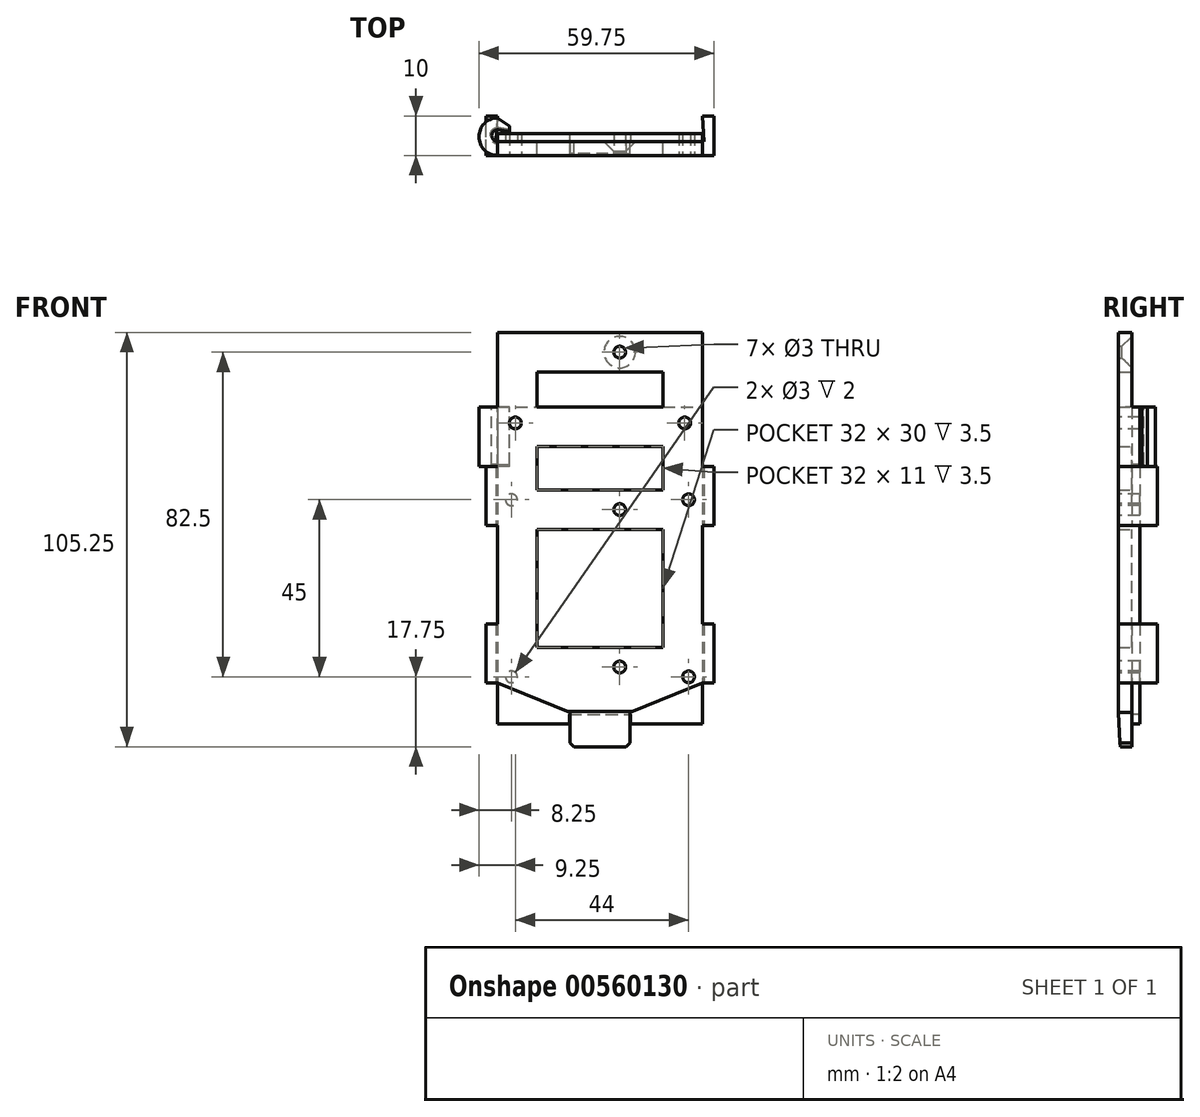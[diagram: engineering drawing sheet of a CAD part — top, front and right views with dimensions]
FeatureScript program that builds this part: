
annotation { "Feature Type Name" : "Feature", "Feature Type Description" : "" }
export const myFeature = defineFeature(function(context is Context, id is Id, definition is map)
    precondition{}
    {
        {
            var Q0;
            Q0=qCreatedBy(makeId("Front.planeOp"),FACE);
            var sketch = newSketch(context, id + "F0", { "sketchPlane" : qUnion([Q0])});
            skLineSegment(sketch, "E0.bottom", {"start": v(26, 40.25) * mm, "end": v(-26, 40.25) * mm});
            skLineSegment(sketch, "E0.top", {"start": v(26, -40.25) * mm, "end": v(-26, -40.25) * mm});
            skLineSegment(sketch, "E0.left", {"start": v(26, 40.25) * mm, "end": v(26, -40.25) * mm});
            skLineSegment(sketch, "E0.right", {"start": v(-26, 40.25) * mm, "end": v(-26, -40.25) * mm});
            skPoint(sketch, "E0.middle", {"position": v(0, 0) * mm});
            skCircle(sketch, "E1", {"center": v(-21.5, 36.25) * mm, "radius": 1.5 * mm});
            skCircle(sketch, "E2", {"center": v(-22.5, 16.75) * mm, "radius": 1.5 * mm});
            skCircle(sketch, "E3", {"center": v(-22.5, -28.25) * mm, "radius": 1.5 * mm});
            skCircle(sketch, "E4.MirrorC", {"center": v(22.5, -28.25) * mm, "radius": 1.5 * mm});
            skCircle(sketch, "E5.MirrorC", {"center": v(22.5, 16.75) * mm, "radius": 1.5 * mm});
            skCircle(sketch, "E6.MirrorC", {"center": v(21.5, 36.25) * mm, "radius": 1.5 * mm});
            skLineSegment(sketch, "E7.bottom", {"start": v(-7.75, -37.75) * mm, "end": v(7.75, -37.75) * mm});
            skLineSegment(sketch, "E7.top", {"start": v(-7.75, -40.25) * mm, "end": v(7.75, -40.25) * mm});
            skLineSegment(sketch, "E7.left", {"start": v(-7.75, -37.75) * mm, "end": v(-7.75, -40.25) * mm});
            skLineSegment(sketch, "E7.right", {"start": v(7.75, -37.75) * mm, "end": v(7.75, -40.25) * mm});
            skCircle(sketch, "E8", {"center": v(5, 14.25) * mm, "radius": 1.5 * mm});
            skCircle(sketch, "E9", {"center": v(5, -25.75) * mm, "radius": 1.5 * mm});
            skSolve(sketch);
        }
        {
            var Q0;
            Q0=makeQuery(id+"F0.imprint","IMPRINT",FACE,{"disambiguationData":[TD([[makeQuery(id+"F0.imprint","IMPRINT",EDGE,{"derivedFrom":sQuery(id+"F0.wireOp",EDGE,"E0.bottom")}),1.0]])]});
            extrude(context, id + "F1", {"entities" : qUnion([Q0]), "oppositeDirection" : true, "depth" : 2 * mm, "offsetDistance" : 25 * mm});
        }
        {
            var Q0;
            Q0=makeQuery(id+"F1.opExtrude","CAP_FACE",FACE,{"disambiguationData":[OSD([sQuery(id+"F0.wireOp",EDGE,"E0.bottom"),sQuery(id+"F0.wireOp",EDGE,"E0.top"),sQuery(id+"F0.wireOp",EDGE,"E0.left"),sQuery(id+"F0.wireOp",EDGE,"E0.right"),sQuery(id+"F0.wireOp",EDGE,"E1"),sQuery(id+"F0.wireOp",EDGE,"E2"),sQuery(id+"F0.wireOp",EDGE,"E3"),sQuery(id+"F0.wireOp",EDGE,"E4.MirrorC"),sQuery(id+"F0.wireOp",EDGE,"E5.MirrorC"),sQuery(id+"F0.wireOp",EDGE,"E6.MirrorC"),sQuery(id+"F0.wireOp",EDGE,"E7.bottom"),sQuery(id+"F0.wireOp",EDGE,"E7.left"),sQuery(id+"F0.wireOp",EDGE,"E7.right")])],"isStart":true});
            var sketch = newSketch(context, id + "F2", { "sketchPlane" : qUnion([Q0])});
            skLineSegment(sketch, "E10.top", {"start": v(-26, 40.25) * mm, "end": v(26, 40.25) * mm});
            skLineSegment(sketch, "E10.left", {"start": v(-26, -29.75) * mm, "end": v(-26, 40.25) * mm});
            skLineSegment(sketch, "E10.right", {"start": v(26, -29.75) * mm, "end": v(26, 40.25) * mm});
            skLineSegment(sketch, "E11", {"start": v(-26, -29.75) * mm, "end": v(-7.65, -37.25) * mm});
            skLineSegment(sketch, "E12", {"start": v(-7.65, -37.25) * mm, "end": v(-7.65, -46) * mm});
            skLineSegment(sketch, "E13", {"start": v(-7.65, -46) * mm, "end": v(0, -46) * mm});
            skLineSegment(sketch, "E14.MirrorCS", {"start": v(26, -29.75) * mm, "end": v(7.65, -37.25) * mm});
            skLineSegment(sketch, "E15.MirrorCS", {"start": v(7.65, -37.25) * mm, "end": v(7.65, -46) * mm});
            skLineSegment(sketch, "E16.MirrorCS", {"start": v(7.65, -46) * mm, "end": v(0, -46) * mm});
            skLineSegment(sketch, "E17.0", {"start": v(-16, -20.75) * mm, "end": v(-16, 30.25) * mm});
            skLineSegment(sketch, "E17.2", {"start": v(-16, 30.25) * mm, "end": v(16, 30.25) * mm});
            skLineSegment(sketch, "E17.5", {"start": v(16, -20.75) * mm, "end": v(16, 9.25) * mm});
            skCircle(sketch, "E18", {"center": v(5, 14.25) * mm, "radius": 1.5 * mm});
            skCircle(sketch, "E19", {"center": v(5, -25.75) * mm, "radius": 1.5 * mm});
            skLineSegment(sketch, "E20.bottom", {"start": v(16, 19.25) * mm, "end": v(-21, 19.25) * mm});
            skLineSegment(sketch, "E20.top", {"start": v(16, 9.25) * mm, "end": v(-16, 9.25) * mm});
            skLineSegment(sketch, "E20.left", {"start": v(16, 19.25) * mm, "end": v(16, 9.25) * mm});
            skLineSegment(sketch, "E21.trimOffspring", {"start": v(16, 19.25) * mm, "end": v(16, 30.25) * mm});
            skLineSegment(sketch, "E22", {"start": v(16, -20.75) * mm, "end": v(-16, -20.75) * mm});
            skSolve(sketch);
        }
        {
            var Q0;
            Q0=qCreatedBy(makeId("Front.planeOp"),FACE);
            var sketch = newSketch(context, id + "F3", { "sketchPlane" : qUnion([Q0])});
            skLineSegment(sketch, "E23.bottom", {"start": v(-26, 40.25) * mm, "end": v(26, 40.25) * mm});
            skLineSegment(sketch, "E23.top", {"start": v(-26, 59.25) * mm, "end": v(26, 59.25) * mm});
            skLineSegment(sketch, "E23.left", {"start": v(-26, 40.25) * mm, "end": v(-26, 59.25) * mm});
            skLineSegment(sketch, "E23.right", {"start": v(26, 40.25) * mm, "end": v(26, 59.25) * mm});
            skCircle(sketch, "E24", {"center": v(5, 54.25) * mm, "radius": 1.5 * mm});
            skLineSegment(sketch, "E25.bottom", {"start": v(-16, 49.25) * mm, "end": v(16, 49.25) * mm});
            skLineSegment(sketch, "E25.top", {"start": v(-16, 40.25) * mm, "end": v(16, 40.25) * mm});
            skLineSegment(sketch, "E25.left", {"start": v(-16, 49.25) * mm, "end": v(-16, 40.25) * mm});
            skLineSegment(sketch, "E25.right", {"start": v(16, 49.25) * mm, "end": v(16, 40.25) * mm});
            skSolve(sketch);
        }
        {
            var Q0;
            {var subQ0=sQuery(id+"F2.wireOp",EDGE,"E13");Q0=makeQuery(id+"F2.imprint","IMPRINT",FACE,{"disambiguationData":[TD([[makeQuery(id+"F2.imprint","IMPRINT",EDGE,{"derivedFrom":subQ0}),1.0]])]});}
            var Q1;
            {var subQ0=sQuery(id+"F2.wireOp",EDGE,"E10.top");Q1=makeQuery(id+"F2.imprint","IMPRINT",FACE,{"disambiguationData":[TD([[makeQuery(id+"F2.imprint","IMPRINT",EDGE,{"derivedFrom":subQ0}),-1.0]])]});}
            var Q2;
            {var subQ6=sQuery(id+"F2.wireOp",EDGE,"E11");Q2=makeQuery(id+"F2.imprint","IMPRINT",FACE,{"disambiguationData":[TD([[makeQuery(id+"F2.imprint","IMPRINT",EDGE,{"derivedFrom":subQ6}),1.0]])]});}
            var Q3;
            {var subQ0=sQuery(id+"F2.wireOp",EDGE,"E12");var subQ1=sQuery(id+"F2.wireOp",EDGE,"E10.bottom");var subQ2=makeQuery(id+"F2.imprint","INTERSECT",VERTEX,{"derivedFrom":[subQ1,subQ0]});Q3=makeQuery(id+"F2.imprint","IMPRINT",FACE,{"disambiguationData":[TD([[makeQuery(id+"F2.imprint","IMPRINT",EDGE,{"disambiguationData":[TD([[subQ2,-1.0]])],"derivedFrom":subQ1}),1.0]])]});}
            var Q4;
            Q4=makeQuery(id+"F2.imprint","IMPRINT",FACE,{"disambiguationData":[TD([[makeQuery(id+"F2.imprint","IMPRINT",EDGE,{"derivedFrom":makeQuery(id+"F1.opExtrude","CAP_EDGE",EDGE,{"disambiguationData":[OSD([sQuery(id+"F0.wireOp",EDGE,"E2")])],"isStart":true})}),1.0]])]});
            var Q5;
            Q5=makeQuery(id+"F2.imprint","IMPRINT",FACE,{"disambiguationData":[TD([[makeQuery(id+"F2.imprint","IMPRINT",EDGE,{"derivedFrom":makeQuery(id+"F1.opExtrude","CAP_EDGE",EDGE,{"disambiguationData":[OSD([sQuery(id+"F0.wireOp",EDGE,"E5.MirrorC")])],"isStart":true})}),-1.0]])]});
            var Q6;
            Q6=makeQuery(id+"F2.imprint","IMPRINT",FACE,{"disambiguationData":[TD([[makeQuery(id+"F2.imprint","IMPRINT",EDGE,{"derivedFrom":sQuery(id+"F2.wireOp",EDGE,"E18")}),-1.0]])]});
            var Q7;
            Q7=makeQuery(id+"F2.imprint","IMPRINT",FACE,{"disambiguationData":[TD([[makeQuery(id+"F2.imprint","IMPRINT",EDGE,{"derivedFrom":makeQuery(id+"F1.opExtrude","CAP_EDGE",EDGE,{"disambiguationData":[OSD([sQuery(id+"F0.wireOp",EDGE,"E4.MirrorC")])],"isStart":true})}),-1.0]])]});
            var Q8;
            Q8=makeQuery(id+"F2.imprint","IMPRINT",FACE,{"disambiguationData":[TD([[makeQuery(id+"F2.imprint","IMPRINT",EDGE,{"derivedFrom":makeQuery(id+"F1.opExtrude","CAP_EDGE",EDGE,{"disambiguationData":[OSD([sQuery(id+"F0.wireOp",EDGE,"E3")])],"isStart":true})}),1.0]])]});
            extrude(context, id + "F4", {"entities" : qUnion([Q0, Q1, Q2, Q3, Q4, Q5, Q6, Q7, Q8]), "depth" : 3.5 * mm, "offsetDistance" : 25 * mm});
        }
        {
            var Q0;
            Q0=makeQuery(id+"F4.opExtrude","CAP_EDGE",EDGE,{"disambiguationData":[OSD([sQuery(id+"F2.wireOp",EDGE,"E13"),sQuery(id+"F2.wireOp",EDGE,"E16.MirrorCS")])],"isStart":false});
            chamfer(context, id + "F5", {"entities" : qUnion([Q0]), "chamferType" : ChamferType.TWO_OFFSETS, "width1" : 9 * mm, "oppositeDirection" : false, "width2" : 0.5 * mm, "tangentPropagation" : true});
        }
        {
            var Q0;
            Q0=makeQuery(id+"F4.opExtrude","SWEPT_EDGE",EDGE,{"disambiguationData":[OSD([sQuery(id+"F2.wireOp",EDGE,"E12"),sQuery(id+"F2.wireOp",EDGE,"E13")])]});
            var Q1;
            Q1=makeQuery(id+"F4.opExtrude","SWEPT_EDGE",EDGE,{"disambiguationData":[OSD([sQuery(id+"F2.wireOp",EDGE,"E15.MirrorCS"),sQuery(id+"F2.wireOp",EDGE,"E16.MirrorCS")])]});
            chamfer(context, id + "F6", {"entities" : qUnion([Q0, Q1]), "width" : 1 * mm, "tangentPropagation" : true});
        }
        {
            var Q0;
            Q0=makeQuery(id+"F4.opExtrude","SWEPT_FACE",FACE,{"disambiguationData":[OSD([sQuery(id+"F2.wireOp",EDGE,"E10.top")])]});
            var sketch = newSketch(context, id + "F7", { "sketchPlane" : qUnion([Q0])});
            skLineSegment(sketch, "E26", {"start": v(-23, 2.5) * mm, "end": v(-25.9, 3) * mm});
            skArc(sketch, "E27", {"start": v(-26, 6) * mm, "mid": v(-30.75, 1.25) * mm, "end": v(-26, -3.5) * mm});
            skLineSegment(sketch, "E28", {"start": v(-23, 2.5) * mm, "end": v(-23, 3.95) * mm});
            skLineSegment(sketch, "E29", {"start": v(-23, 3.95) * mm, "end": v(-26, 6) * mm});
            skPoint(sketch, "E30.center.orphan", {"position": v(-26, 1.5) * mm});
            skArc(sketch, "E31", {"start": v(-25.9, 3) * mm, "mid": v(-27.5, 1.55) * mm, "end": v(-26, 0) * mm});
            skArc(sketch, "E32.MirrorCS", {"start": v(26, 6) * mm, "mid": v(30.75, 1.25) * mm, "end": v(26, -3.5) * mm});
            skArc(sketch, "E33.MirrorCS", {"start": v(25.9, 3) * mm, "mid": v(27.5, 1.55) * mm, "end": v(26, 0) * mm});
            skLineSegment(sketch, "E34.MirrorCS", {"start": v(23, 2.5) * mm, "end": v(25.9, 3) * mm});
            skLineSegment(sketch, "E35.MirrorCS", {"start": v(23, 3.95) * mm, "end": v(26, 6) * mm});
            skLineSegment(sketch, "E36.MirrorCS", {"start": v(23, 2.5) * mm, "end": v(23, 3.95) * mm});
            skSolve(sketch);
        }
        {
            var Q0;
            Q0=qSketchRegion(id+"F7",true);
            var Q1;
            Q1=makeQuery(id+"F7.imprint","IMPRINT",FACE,{"disambiguationData":[TD([[makeQuery(id+"F7.imprint","IMPRINT",EDGE,{"derivedFrom":sQuery(id+"F7.wireOp",EDGE,"E26")}),-1.0]])]});
            var Q2;
            Q2=makeQuery(id+"F7.imprint","IMPRINT",FACE,{"disambiguationData":[TD([[makeQuery(id+"F7.imprint","IMPRINT",EDGE,{"derivedFrom":sQuery(id+"F7.wireOp",EDGE,"E32.MirrorCS")}),-1.0]])]});
            extrude(context, id + "F8", {"entities" : qUnion([Q0, Q1, Q2]), "operationType" : NewBodyOperationType.ADD, "oppositeDirection" : true, "depth" : 15 * mm, "offsetDistance" : 25 * mm});
        }
        {
            var Q0;
            Q0=makeQuery(id+"F3.imprint","IMPRINT",FACE,{"disambiguationData":[TD([[makeQuery(id+"F3.imprint","IMPRINT",EDGE,{"derivedFrom":sQuery(id+"F3.wireOp",EDGE,"E23.top")}),-1.0]])]});
            var Q1;
            Q1=makeQuery(id+"F4.opExtrude","CAP_FACE",FACE,{"disambiguationData":[OSD([sQuery(id+"F0.wireOp",EDGE,"E1"),sQuery(id+"F0.wireOp",EDGE,"E6.MirrorC"),sQuery(id+"F2.wireOp",EDGE,"E10.top"),sQuery(id+"F2.wireOp",EDGE,"E10.left"),sQuery(id+"F2.wireOp",EDGE,"E10.right"),sQuery(id+"F2.wireOp",EDGE,"E11"),sQuery(id+"F2.wireOp",EDGE,"E12"),sQuery(id+"F2.wireOp",EDGE,"E13"),sQuery(id+"F2.wireOp",EDGE,"E14.MirrorCS"),sQuery(id+"F2.wireOp",EDGE,"E15.MirrorCS"),sQuery(id+"F2.wireOp",EDGE,"E16.MirrorCS"),sQuery(id+"F2.wireOp",EDGE,"E17.0"),sQuery(id+"F2.wireOp",EDGE,"E17.2"),sQuery(id+"F2.wireOp",EDGE,"E17.5"),sQuery(id+"F2.wireOp",EDGE,"E18"),sQuery(id+"F2.wireOp",EDGE,"E19"),sQuery(id+"F2.wireOp",EDGE,"E20.bottom"),sQuery(id+"F2.wireOp",EDGE,"E20.top"),sQuery(id+"F2.wireOp",EDGE,"E21.trimOffspring"),sQuery(id+"F2.wireOp",EDGE,"E22")])],"isStart":false});
            extrude(context, id + "F9", {"entities" : qUnion([Q0]), "operationType" : NewBodyOperationType.ADD, "endBound" : BoundingType.UP_TO_SURFACE, "depth" : 25 * mm, "endBoundEntityFace" : qUnion([Q1]), "offsetDistance" : 25 * mm});
        }
        {
            var Q0;
            Q0=makeQuery(id+"F8.opExtrude","CAP_EDGE",EDGE,{"disambiguationData":[OSD([sQuery(id+"F7.wireOp",EDGE,"E26")])],"isStart":false});
            var Q1;
            Q1=makeQuery(id+"F8.opExtrude","CAP_EDGE",EDGE,{"disambiguationData":[OSD([sQuery(id+"F7.wireOp",EDGE,"E31")])],"isStart":false});
            var Q2;
            Q2=makeQuery(id+"F8.opExtrude","CAP_EDGE",EDGE,{"disambiguationData":[OSD([sQuery(id+"F7.wireOp",EDGE,"E34.MirrorCS")])],"isStart":false});
            var Q3;
            Q3=makeQuery(id+"F8.opExtrude","CAP_EDGE",EDGE,{"disambiguationData":[OSD([sQuery(id+"F7.wireOp",EDGE,"E33.MirrorCS")])],"isStart":false});
            chamfer(context, id + "F10", {"entities" : qUnion([Q0, Q1, Q2, Q3]), "width" : .5 * mm, "tangentPropagation" : true});
        }
        {
            var Q0;
            Q0=makeQuery(id+"F4.opExtrude","CAP_FACE",FACE,{"disambiguationData":[OSD([sQuery(id+"F0.wireOp",EDGE,"E1"),sQuery(id+"F0.wireOp",EDGE,"E6.MirrorC"),sQuery(id+"F0.wireOp",EDGE,"E8"),sQuery(id+"F0.wireOp",EDGE,"E9"),sQuery(id+"F2.wireOp",EDGE,"E10.top"),sQuery(id+"F2.wireOp",EDGE,"E10.left"),sQuery(id+"F2.wireOp",EDGE,"E10.right"),sQuery(id+"F2.wireOp",EDGE,"E11"),sQuery(id+"F2.wireOp",EDGE,"E12"),sQuery(id+"F2.wireOp",EDGE,"E13"),sQuery(id+"F2.wireOp",EDGE,"E14.MirrorCS"),sQuery(id+"F2.wireOp",EDGE,"E15.MirrorCS"),sQuery(id+"F2.wireOp",EDGE,"E16.MirrorCS")])],"isStart":true});
            var sketch = newSketch(context, id + "F11", { "sketchPlane" : qUnion([Q0])});
            skLineSegment(sketch, "E37.0", {"start": v(-21, -26.4) * mm, "end": v(-2.65, -33.9) * mm});
            skLineSegment(sketch, "E37.1", {"start": v(-21, 25.75) * mm, "end": v(-21, -26.4) * mm});
            skLineSegment(sketch, "E37.2", {"start": v(-2.65, -33.9) * mm, "end": v(-2.65, -41) * mm});
            skLineSegment(sketch, "E37.3", {"start": v(-21, 35.25) * mm, "end": v(-21, 25.75) * mm});
            skLineSegment(sketch, "E37.4", {"start": v(21, 35.25) * mm, "end": v(-21, 35.25) * mm});
            skLineSegment(sketch, "E37.5", {"start": v(21, 25.75) * mm, "end": v(21, 35.25) * mm});
            skLineSegment(sketch, "E37.6", {"start": v(-2.65, -41) * mm, "end": v(2.65, -41) * mm});
            skLineSegment(sketch, "E37.7", {"start": v(2.65, -41) * mm, "end": v(2.65, -33.9) * mm});
            skLineSegment(sketch, "E37.8", {"start": v(2.65, -33.9) * mm, "end": v(21, -26.4) * mm});
            skLineSegment(sketch, "E37.9", {"start": v(21, -26.4) * mm, "end": v(21, 25.75) * mm});
            skLineSegment(sketch, "E38", {"start": v(-23.55, -30.75) * mm, "end": v(23.55, -30.75) * mm});
            skLineSegment(sketch, "E39", {"start": v(-23.55, -30.75) * mm, "end": v(-16.83, -33.5) * mm});
            skLineSegment(sketch, "E40", {"start": v(-16.83, -33.5) * mm, "end": v(16.83, -33.5) * mm});
            skLineSegment(sketch, "E41", {"start": v(16.83, -33.5) * mm, "end": v(23.55, -30.75) * mm});
            skSolve(sketch);
        }
        {
            var Q0;
            {var subQ5=sQuery(id+"F11.wireOp",EDGE,"E39");Q0=makeQuery(id+"F11.imprint","IMPRINT",FACE,{"disambiguationData":[TD([[makeQuery(id+"F11.imprint","IMPRINT",EDGE,{"derivedFrom":subQ5}),1.0]])]});}
            var Q1;
            {var subQ5=sQuery(id+"F11.wireOp",EDGE,"E41");Q1=makeQuery(id+"F11.imprint","IMPRINT",FACE,{"disambiguationData":[TD([[makeQuery(id+"F11.imprint","IMPRINT",EDGE,{"derivedFrom":subQ5}),-1.0]])]});}
            extrude(context, id + "F12", {"entities" : qUnion([Q0, Q1]), "operationType" : NewBodyOperationType.ADD, "depth" : .2 * mm, "offsetDistance" : 25 * mm});
        }
        {
            var Q0;
            Q0=makeQuery(id+"F4.opExtrude","SWEPT_FACE",FACE,{"disambiguationData":[OSD([sQuery(id+"F2.wireOp",EDGE,"E10.right")])]});
            var sketch = newSketch(context, id + "F13", { "sketchPlane" : qUnion([Q0])});
            skLineSegment(sketch, "E42.bottom", {"start": v(-3.5, -29.75) * mm, "end": v(6.5, -29.75) * mm});
            skLineSegment(sketch, "E42.top", {"start": v(-3.5, -14.75) * mm, "end": v(6.5, -14.75) * mm});
            skLineSegment(sketch, "E42.left", {"start": v(-3.5, -29.75) * mm, "end": v(-3.5, -14.75) * mm});
            skLineSegment(sketch, "E42.right", {"start": v(6.5, -29.75) * mm, "end": v(6.5, -14.75) * mm});
            skPoint(sketch, "E43.oppositeSnap0", {"position": v(6.5, -22.25) * mm});
            skLineSegment(sketch, "E43.bottom", {"start": v(-3.5, 10.25) * mm, "end": v(6.5, 10.25) * mm});
            skLineSegment(sketch, "E43.top", {"start": v(-3.5, 25.25) * mm, "end": v(6.5, 25.25) * mm});
            skLineSegment(sketch, "E43.left", {"start": v(-3.5, 10.25) * mm, "end": v(-3.5, 25.25) * mm});
            skLineSegment(sketch, "E43.right", {"start": v(6.5, 10.25) * mm, "end": v(6.5, 25.25) * mm});
            skSolve(sketch);
        }
        {
            var Q0;
            Q0=qSketchRegion(id+"F13",true);
            extrude(context, id + "F14", {"entities" : qUnion([Q0]), "depth" : 3 * mm, "offsetDistance" : 25 * mm});
        }
        {
            var Q0;
            Q0=makeQuery(id+"F14.opExtrude","SWEPT_FACE",FACE,{"disambiguationData":[OSD([sQuery(id+"F13.wireOp",EDGE,"E42.bottom")])]});
            var sketch = newSketch(context, id + "F15", { "sketchPlane" : qUnion([Q0])});
            skLineSegment(sketch, "E44", {"start": v(26, 0) * mm, "end": v(26.47, 0) * mm});
            skLineSegment(sketch, "E45", {"start": v(26.47, 0) * mm, "end": v(26, -6.5) * mm});
            skLineSegment(sketch, "E46", {"start": v(26, -6.5) * mm, "end": v(26, 0) * mm});
            skSolve(sketch);
        }
        {
            var Q0;
            Q0=qSketchRegion(id+"F15",true);
            var Q1;
            Q1=makeQuery(id+"F14.opExtrude","SWEPT_FACE",FACE,{"disambiguationData":[OSD([sQuery(id+"F13.wireOp",EDGE,"E43.top")])]});
            extrude(context, id + "F16", {"entities" : qUnion([Q0]), "operationType" : NewBodyOperationType.REMOVE, "endBound" : BoundingType.UP_TO_SURFACE, "oppositeDirection" : true, "depth" : 25 * mm, "endBoundEntityFace" : qUnion([Q1]), "offsetDistance" : 25 * mm});
        }
        {
            var Q0;
            Q0=makeQuery(id+"F14.opExtrude","SWEPT_BODY",BODY,{"disambiguationData":[OSD([sQuery(id+"F13.wireOp",EDGE,"E42.bottom"),sQuery(id+"F13.wireOp",EDGE,"E42.top"),sQuery(id+"F13.wireOp",EDGE,"E42.left"),sQuery(id+"F13.wireOp",EDGE,"E42.right")])]});
            var Q1;
            Q1=makeQuery(id+"F14.opExtrude","SWEPT_BODY",BODY,{"disambiguationData":[OSD([sQuery(id+"F13.wireOp",EDGE,"E43.bottom"),sQuery(id+"F13.wireOp",EDGE,"E43.top"),sQuery(id+"F13.wireOp",EDGE,"E43.left"),sQuery(id+"F13.wireOp",EDGE,"E43.right")])]});
            var Q2;
            Q2=qCreatedBy(makeId("Right.planeOp"),FACE);
            mirror(context, id + "F17", {"operationType" : NewBodyOperationType.ADD, "entities" : qUnion([Q0, Q1]), "mirrorPlane" : qUnion([Q2])});
        }
        {
            var Q0;
            Q0=makeQuery(id+"F4.opExtrude","CAP_EDGE",EDGE,{"disambiguationData":[OSD([sQuery(id+"F2.wireOp",EDGE,"E18")])],"isStart":true});
            var Q1;
            Q1=makeQuery(id+"F4.opExtrude","CAP_EDGE",EDGE,{"disambiguationData":[OSD([sQuery(id+"F2.wireOp",EDGE,"E19")])],"isStart":true});
            var Q2;
            Q2=makeQuery(id+"F9.opExtrude","CAP_EDGE",EDGE,{"disambiguationData":[OSD([sQuery(id+"F3.wireOp",EDGE,"E24")])],"isStart":true});
            chamfer(context, id + "F18", {"entities" : qUnion([Q0, Q1, Q2]), "width" : 2.5 * mm, "tangentPropagation" : true});
        }
    });
